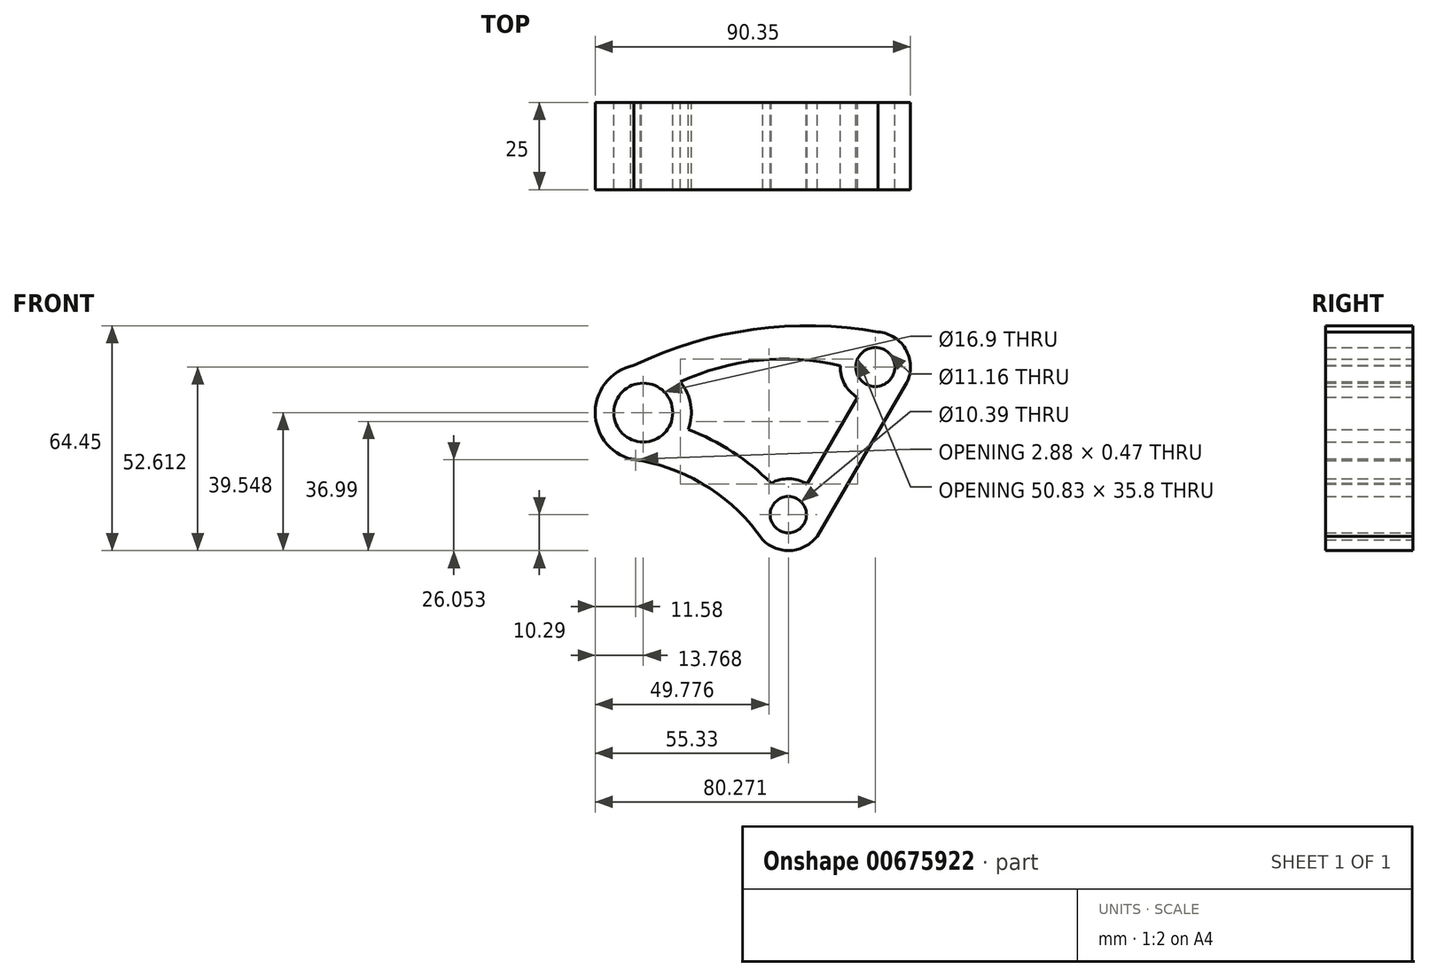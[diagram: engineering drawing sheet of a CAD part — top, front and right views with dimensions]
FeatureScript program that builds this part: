
annotation { "Feature Type Name" : "Feature", "Feature Type Description" : "" }
export const myFeature = defineFeature(function(context is Context, id is Id, definition is map)
    precondition{}
    {
        {
            var Q0;
            Q0=qCreatedBy(makeId("Front.planeOp"),FACE);
            var sketch = newSketch(context, id + "F0", { "sketchPlane" : qUnion([Q0])});
            skArc(sketch, "E0", {"start": v(-7.37, -7.18) * mm, "mid": v(0.68, -10.27) * mm, "end": v(8.25, -6.15) * mm});
            skCircle(sketch, "E1", {"center": v(0, 0) * mm, "radius": 5.2 * mm});
            skArc(sketch, "E2.trimOffspring", {"start": v(5.34, 8.8) * mm, "mid": v(0.14, 10.29) * mm, "end": v(-5.1, 8.94) * mm});
            skCircle(sketch, "E3", {"center": v(-41.56, 29.26) * mm, "radius": 8.45 * mm});
            skCircle(sketch, "E4", {"center": v(24.94, 42.32) * mm, "radius": 5.58 * mm});
            skArc(sketch, "E5", {"start": v(14.87, 42.72) * mm, "mid": v(16.1, 37.48) * mm, "end": v(19.86, 33.61) * mm});
            skArc(sketch, "E6", {"start": v(-44.34, 42.72) * mm, "mid": v(-55.27, 28.24) * mm, "end": v(-42.31, 15.53) * mm});
            skLineSegment(sketch, "E7", {"start": v(8.25, -6.15) * mm, "end": v(33.64, 37.23) * mm});
            skLineSegment(sketch, "E8", {"start": v(5.34, 8.8) * mm, "end": v(19.86, 33.61) * mm});
            skArc(sketch, "E9", {"start": v(27.89, 51.96) * mm, "mid": v(-8.98, 53.23) * mm, "end": v(-44.34, 42.72) * mm});
            skArc(sketch, "E10", {"start": v(14.87, 42.72) * mm, "mid": v(-8.46, 44.25) * mm, "end": v(-31, 38.05) * mm});
            skArc(sketch, "E11.trimOffspring", {"start": v(33.64, 37.23) * mm, "mid": v(33.87, 47) * mm, "end": v(25.7, 52.37) * mm});
            skArc(sketch, "E12.trimOffspring", {"start": v(-27.83, 28.53) * mm, "mid": v(-28.51, 33.59) * mm, "end": v(-31, 38.05) * mm});
            skArc(sketch, "E13", {"start": v(-7.37, -7.18) * mm, "mid": v(-23.84, 8.4) * mm, "end": v(-45.19, 16) * mm});
            skArc(sketch, "E14.trimOffspring", {"start": v(-4.93, 9.03) * mm, "mid": v(-15.98, 17.98) * mm, "end": v(-28.67, 24.41) * mm});
            skPoint(sketch, "E15.orphan", {"position": v(0.42, 5.18) * mm});
            skPoint(sketch, "E16.start.orphan", {"position": v(0.42, -0.14) * mm});
            skArc(sketch, "E17", {"start": v(-28.67, 24.41) * mm, "mid": v(-27.98, 31.54) * mm, "end": v(-30.97, 38.06) * mm});
            skArc(sketch, "E18.trimOffspring", {"start": v(-44.25, 42.76) * mm, "mid": v(-55.3, 28.2) * mm, "end": v(-42.15, 15.5) * mm});
            skSolve(sketch);
        }
        {
            var Q0;
            Q0 = qSketchRegion(id + "F0", true);
            extrude(context, id + "F1", {"entities" : qUnion([Q0]), "depth" : 25 * mm, "offsetDistance" : 25 * mm});
        }
    });
